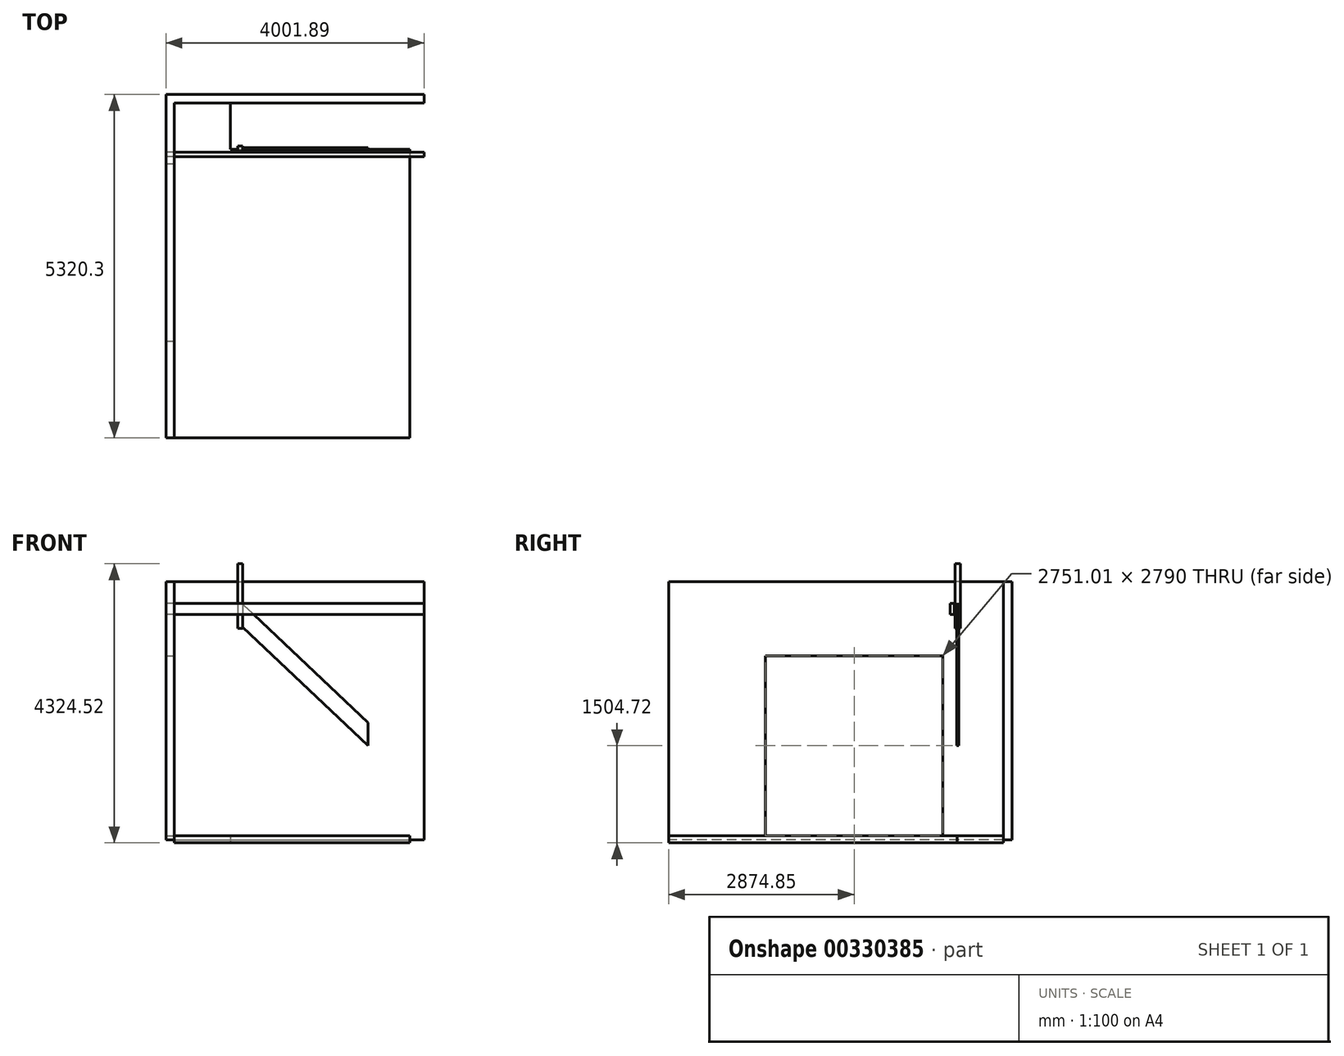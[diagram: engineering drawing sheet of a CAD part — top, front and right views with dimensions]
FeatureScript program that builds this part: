
annotation { "Feature Type Name" : "Feature", "Feature Type Description" : "" }
export const myFeature = defineFeature(function(context is Context, id is Id, definition is map)
    precondition{}
    {
        {
            var Q0;
            Q0=qCreatedBy(makeId("Top.planeOp"),FACE);
            var sketch = newSketch(context, id + "F0", { "sketchPlane" : qUnion([Q0])});
            skLineSegment(sketch, "E0", {"start": v(-1310.06, 4531) * mm, "end": v(-445.06, 4531) * mm});
            skLineSegment(sketch, "E1", {"start": v(-445.06, 4531) * mm, "end": v(-445.06, 3811) * mm});
            skLineSegment(sketch, "E2", {"start": v(-445.06, 3811) * mm, "end": v(2339.94, 3811) * mm});
            skLineSegment(sketch, "E3", {"start": v(2339.94, 3811) * mm, "end": v(2339.94, -659) * mm});
            skLineSegment(sketch, "E4", {"start": v(2339.94, -659) * mm, "end": v(-1310.06, -659) * mm});
            skLineSegment(sketch, "E5", {"start": v(-1310.06, -659) * mm, "end": v(-1310.06, 4531) * mm});
            skSolve(sketch);
        }
        {
            var Q0;
            Q0 = qSketchRegion(id + "F0", true);
            extrude(context, id + "F1", {"entities" : qUnion([Q0]), "depth" : 60 * mm});
        }
        {
            var Q0;
            Q0=qCreatedBy(makeId("Top.planeOp"),FACE);
            var sketch = newSketch(context, id + "F2", { "sketchPlane" : qUnion([Q0])});
            skLineSegment(sketch, "E6.bottom", {"start": v(-1440.1, 4531.29) * mm, "end": v(2559.9, 4531.29) * mm});
            skLineSegment(sketch, "E6.top", {"start": v(-1440.1, 4661.29) * mm, "end": v(2559.9, 4661.29) * mm});
            skLineSegment(sketch, "E6.left", {"start": v(-1440.1, 4531.29) * mm, "end": v(-1440.1, 4661.29) * mm});
            skLineSegment(sketch, "E6.right", {"start": v(2559.9, 4531.29) * mm, "end": v(2559.9, 4661.29) * mm});
            skLineSegment(sketch, "E7.bottom", {"start": v(-1310.07, 4533.1) * mm, "end": v(-1440.07, 4533.1) * mm});
            skLineSegment(sketch, "E7.top", {"start": v(-1310.07, -659.01) * mm, "end": v(-1440.07, -659.01) * mm});
            skLineSegment(sketch, "E7.left", {"start": v(-1310.07, 4533.1) * mm, "end": v(-1310.07, -659.01) * mm});
            skLineSegment(sketch, "E7.right", {"start": v(-1440.07, 4533.1) * mm, "end": v(-1440.07, -659.01) * mm});
            skSolve(sketch);
        }
        {
            var Q0;
            Q0 = qSketchRegion(id + "F2", true);
            extrude(context, id + "F3", {"entities" : qUnion([Q0]), "depth" : 4000 * mm});
        }
        {
            var Q0;
            Q0=qCreatedBy(makeId("Right.planeOp"),FACE);
            var sketch = newSketch(context, id + "F4", { "sketchPlane" : qUnion([Q0])});
            skLineSegment(sketch, "E8.right", {"start": v(840.33, 59.72) * mm, "end": v(840.33, 2249.2) * mm});
            skLineSegment(sketch, "E9.right", {"start": v(3591.34, 60.24) * mm, "end": v(3591.34, 2849.72) * mm});
            skLineSegment(sketch, "E10.bottom", {"start": v(840.33, 59.72) * mm, "end": v(3591.34, 59.72) * mm});
            skLineSegment(sketch, "E10.top", {"start": v(840.33, 2849.72) * mm, "end": v(3591.34, 2849.72) * mm});
            skLineSegment(sketch, "E10.left", {"start": v(840.33, 59.72) * mm, "end": v(840.33, 2849.72) * mm});
            skLineSegment(sketch, "E10.right", {"start": v(3591.34, 59.72) * mm, "end": v(3591.34, 2849.72) * mm});
            skSolve(sketch);
        }
        {
            var Q0;
            {var subQ0=sQuery(id+"F4.wireOp",EDGE,"E10.bottom");Q0=makeQuery(id+"F4.imprint","IMPRINT",FACE,{"disambiguationData":[TD([[makeQuery(id+"F4.imprint","IMPRINT",EDGE,{"derivedFrom":subQ0}),1.0]])]});}
            extrude(context, id + "F5", {"entities" : qUnion([Q0]), "oppositeDirection" : true, "depth" : 3110 * mm});
        }
        {
            var Q0;
            Q0=makeQuery(id+"F5.opExtrude","SWEPT_BODY",BODY,{"disambiguationData":[OSD([sQuery(id+"F4.wireOp",EDGE,"E10.bottom"),sQuery(id+"F4.wireOp",EDGE,"E10.top"),sQuery(id+"F4.wireOp",EDGE,"E10.left"),sQuery(id+"F4.wireOp",EDGE,"E10.right")])]});
            var Q1;
            Q1=makeQuery(id+"F3.opExtrude","SWEPT_BODY",BODY,{"disambiguationData":[OSD([sQuery(id+"F2.wireOp",EDGE,"E6.bottom"),sQuery(id+"F2.wireOp",EDGE,"E6.top"),sQuery(id+"F2.wireOp",EDGE,"E6.left"),sQuery(id+"F2.wireOp",EDGE,"E6.right"),sQuery(id+"F2.wireOp",EDGE,"E7.top"),sQuery(id+"F2.wireOp",EDGE,"E7.left"),sQuery(id+"F2.wireOp",EDGE,"E7.right")])]});
            booleanBodies(context, id + "F6", {"operationType" : BooleanOperationType.SUBTRACTION, "tools" : qUnion([Q0]), "targets" : qUnion([Q1])});
        }
        {
            var Q0;
            Q0=qCreatedBy(makeId("Front.planeOp"),FACE);
            var sketch = newSketch(context, id + "F7", { "sketchPlane" : qUnion([Q0])});
            skLineSegment(sketch, "E11.bottom", {"start": v(0, 0) * mm, "end": v(-481.5, 0) * mm});
            skLineSegment(sketch, "E11.top", {"start": v(2558.01, 3490) * mm, "end": v(-481.5, 3490) * mm});
            skLineSegment(sketch, "E12.bottom", {"start": v(2558.01, 3490) * mm, "end": v(-1441.99, 3490) * mm});
            skLineSegment(sketch, "E12.top", {"start": v(2558.01, 3660) * mm, "end": v(-1441.99, 3660) * mm});
            skLineSegment(sketch, "E12.left", {"start": v(2558.01, 3490) * mm, "end": v(2558.01, 3660) * mm});
            skLineSegment(sketch, "E12.right", {"start": v(-1441.99, 3490) * mm, "end": v(-1441.99, 3660) * mm});
            skSolve(sketch);
        }
        {
            var Q0;
            Q0 = qSketchRegion(id + "F7", true);
            extrude(context, id + "F8", {"entities" : qUnion([Q0]), "endBound" : BoundingType.SYMMETRIC, "depth" : 65 * mm});
        }
        {
            var Q0;
            Q0=makeQuery(id+"F8.opExtrude","SWEPT_BODY",BODY,{"disambiguationData":[OSD([sQuery(id+"F7.wireOp",EDGE,"E12.bottom"),sQuery(id+"F7.wireOp",EDGE,"E12.top"),sQuery(id+"F7.wireOp",EDGE,"E12.left"),sQuery(id+"F7.wireOp",EDGE,"E12.right")])]});
            transform(context, id + "F9", {"entities" : qUnion([Q0]), "transformType" : TransformType.TRANSLATION_3D, "dx" : 0 * mm, "dy" : 3734.4 * mm, "dz" : 0 * mm, "makeCopy" : false});
        }
        {
            var Q0;
            Q0 = qSketchRegion(id + "F0", true);
            extrude(context, id + "F10", {"entities" : qUnion([Q0]), "operationType" : NewBodyOperationType.ADD, "oppositeDirection" : true, "depth" : 50 * mm});
        }
        {
            var Q0;
            Q0=qCreatedBy(makeId("Front.planeOp"),FACE);
            var sketch = newSketch(context, id + "F11", { "sketchPlane" : qUnion([Q0])});
            skLineSegment(sketch, "E13", {"start": v(0, 0) * mm, "end": v(0, 355) * mm});
            skLineSegment(sketch, "E14", {"start": v(0, 355) * mm, "end": v(-1939.95, 2189.52) * mm});
            skLineSegment(sketch, "E15", {"start": v(-1939.95, 2189.52) * mm, "end": v(-1939.95, 1834.52) * mm});
            skLineSegment(sketch, "E16", {"start": v(-1939.95, 1834.52) * mm, "end": v(0, 0) * mm});
            skSolve(sketch);
        }
        {
            var Q0;
            Q0 = qSketchRegion(id + "F11", true);
            extrude(context, id + "F12", {"entities" : qUnion([Q0]), "depth" : 30 * mm});
        }
        {
            var Q0;
            Q0=makeQuery(id+"F12.opExtrude","SWEPT_BODY",BODY,{"disambiguationData":[OSD([sQuery(id+"F11.wireOp",EDGE,"E13"),sQuery(id+"F11.wireOp",EDGE,"E14"),sQuery(id+"F11.wireOp",EDGE,"E15"),sQuery(id+"F11.wireOp",EDGE,"E16")])]});
            transform(context, id + "F13", {"entities" : qUnion([Q0]), "transformType" : TransformType.TRANSLATION_3D, "dx" : 1690 * mm, "dy" : 3836.29 * mm, "dz" : 1460 * mm, "makeCopy" : false});
        }
        {
            var Q0;
            Q0=qCreatedBy(makeId("Top.planeOp"),FACE);
            var sketch = newSketch(context, id + "F14", { "sketchPlane" : qUnion([Q0])});
            skLineSegment(sketch, "E17.bottom", {"start": v(40, -40) * mm, "end": v(-40, -40) * mm});
            skLineSegment(sketch, "E17.top", {"start": v(40, 40) * mm, "end": v(-40, 40) * mm});
            skLineSegment(sketch, "E17.left", {"start": v(40, -40) * mm, "end": v(40, 40) * mm});
            skLineSegment(sketch, "E17.right", {"start": v(-40, -40) * mm, "end": v(-40, 40) * mm});
            skPoint(sketch, "E17.middle", {"position": v(0, 0) * mm});
            skSolve(sketch);
        }
        {
            var Q0;
            Q0 = qSketchRegion(id + "F14", true);
            extrude(context, id + "F15", {"entities" : qUnion([Q0]), "depth" : 1000 * mm});
        }
        {
            var Q0;
            Q0=makeQuery(id+"F15.opExtrude","SWEPT_BODY",BODY,{"disambiguationData":[OSD([sQuery(id+"F14.wireOp",EDGE,"E17.bottom"),sQuery(id+"F14.wireOp",EDGE,"E17.top"),sQuery(id+"F14.wireOp",EDGE,"E17.left"),sQuery(id+"F14.wireOp",EDGE,"E17.right")])]});
            transform(context, id + "F16", {"entities" : qUnion([Q0]), "transformType" : TransformType.TRANSLATION_3D, "dx" : -289.95 * mm, "dy" : 3821.29 * mm, "dz" : 3274.52 * mm, "makeCopy" : false});
        }
    });
